# Revit family: Trane_TVR_Indoor_Floor standing_4TVS0018(24,27)EF000AA(2nd DC)
name_source: partatom
category: Equipamento mecânico
units: mm (PartAtom-declared; Revit-internal decimal feet)

## family parameters
Com base no plano de trabalho = Não
Compartilhado = Não
Corte com vazios quando carregada = Não
Cota do conector redondo = Utilizar diâmetro
Número OmniClass = 23.75.00.00
Ponto de cálculo do ambiente = Não
Sempre na vertical = Sim
Tipo de parte = Normal
Título OmniClass = Climate Control (HVAC)

## types (3) — shared parameters
Condensation = air
Depth = 212  [stored 0.695538 ft]
Descrição = High efficiency air cooled
Drain pipe = 16  [stored 0.0524934 ft]
Fabricante = Trane
Gas = R410a
Gas pipe = 15.9  [stored 0.0521654 ft]
Height = 545  [stored 1.78806 ft]
Installation = Indoor installation
Liquid pipe = 9.53
Machine material = grilles：ABS/HIPS
Maximum Fuse Amps = 15.000 A
Power supply = 220-240V ~50/60Hz
Series = TVR ULTRA
URL = https://www.trane.com
Width = 1340  [stored 4.39633 ft]

## per-type parameters (varying)
| type | Air Flow | Cooling Capacity | Cooling Power Input | Heating Capacity | Heating Power Input | Minimum Circuit Amps | Net Weight |
| 4TVS0024EF000AA | 1380/1290/1205/1100/1033/955/870m3/h | 7 kW | 110 W | 8 kW | 110 W | 1.400 A | 30.50 kg |
| 4TVS0027EF000AA | 1380/1290/1205/1100/1033/955/870m3/h | 8 kW | 130 W | 9 kW | 130 W | 1.400 A | 32.00 kg |
| 4TVS0018EF000AA | 1150/1094/1028/970/925/886/830m3/h | 6 kW | 88 W | 6 kW | 88 W | 0.850 A | 30.50 kg |

note: column(s) folded — value = type name in every type: Modelo

note: [stored X ft] marks values corroborated as IEEE doubles in the binary element streams (Revit-internal decimal feet)

## geometry (parser evidence)
native form markers: Blend x2, Sweep x6
no freeform markers — native parametric forms only
